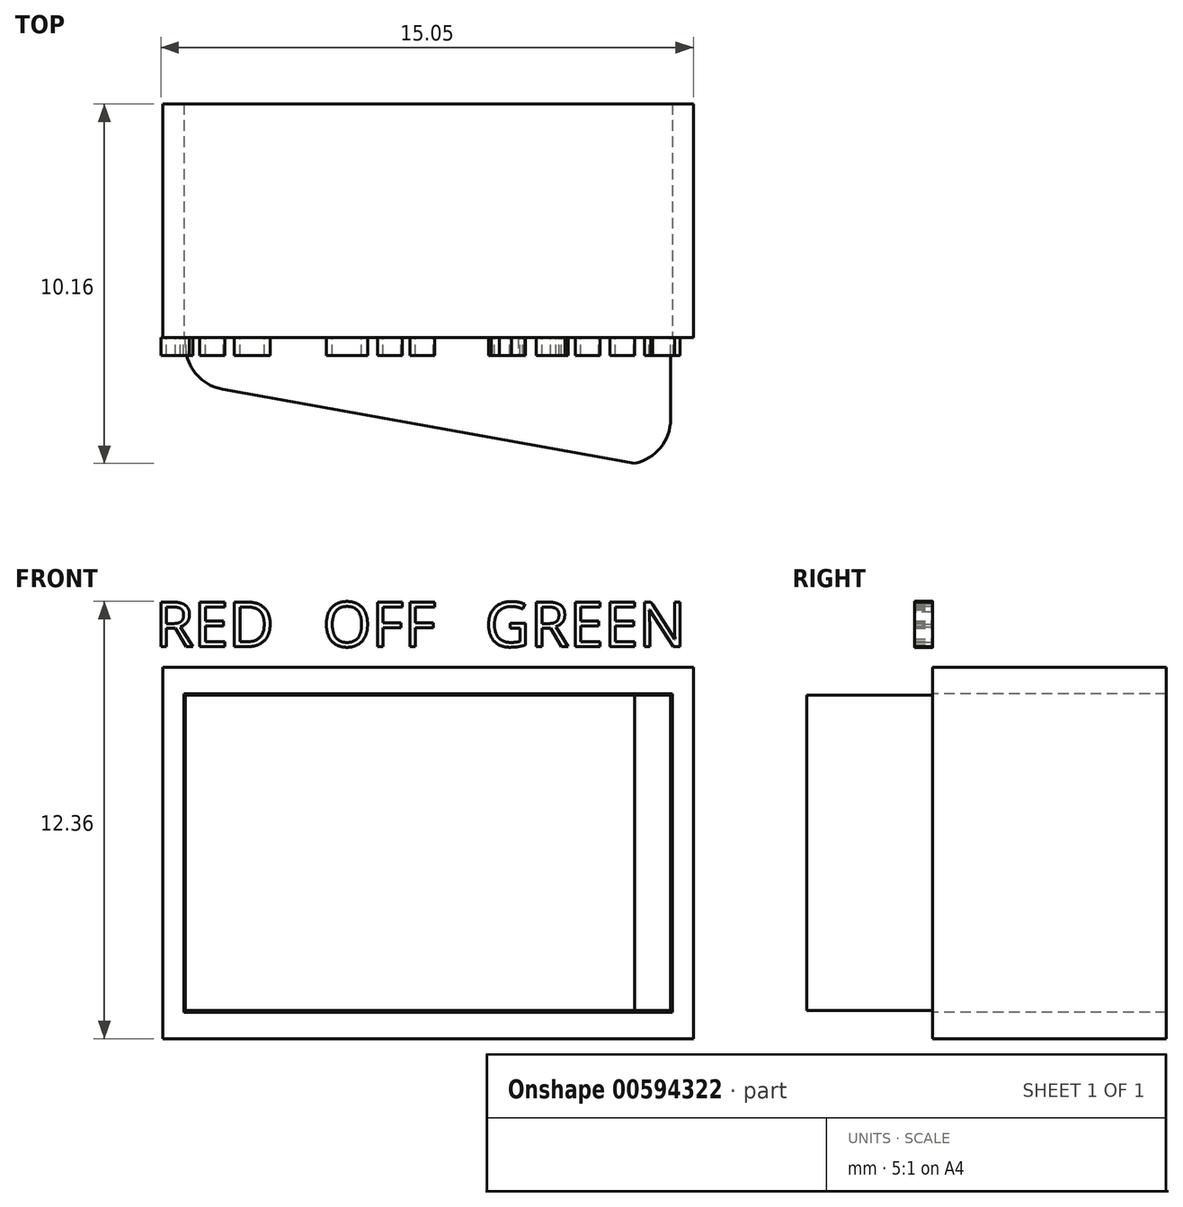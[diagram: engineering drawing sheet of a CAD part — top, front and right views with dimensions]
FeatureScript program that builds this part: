
annotation { "Feature Type Name" : "Feature", "Feature Type Description" : "" }
export const myFeature = defineFeature(function(context is Context, id is Id, definition is map)
    precondition{}
    {
        {
            var Q0;
            Q0=qCreatedBy(makeId("Front.planeOp"),FACE);
            var sketch = newSketch(context, id + "F0", { "sketchPlane" : qUnion([Q0])});
            skLineSegment(sketch, "E0.bottom", {"start": v(-6.9, -4.5) * mm, "end": v(6.9, -4.5) * mm});
            skLineSegment(sketch, "E0.top", {"start": v(-6.9, 4.5) * mm, "end": v(6.9, 4.5) * mm});
            skLineSegment(sketch, "E0.left", {"start": v(-6.9, -4.5) * mm, "end": v(-6.9, 4.5) * mm});
            skLineSegment(sketch, "E0.right", {"start": v(6.9, -4.5) * mm, "end": v(6.9, 4.5) * mm});
            skPoint(sketch, "E0.middle", {"position": v(0, 0) * mm});
            skLineSegment(sketch, "E1.bottom", {"start": v(-7.5, -5.25) * mm, "end": v(7.5, -5.25) * mm});
            skLineSegment(sketch, "E1.top", {"start": v(-7.5, 5.25) * mm, "end": v(7.5, 5.25) * mm});
            skLineSegment(sketch, "E1.left", {"start": v(-7.5, -5.25) * mm, "end": v(-7.5, 5.25) * mm});
            skLineSegment(sketch, "E1.right", {"start": v(7.5, -5.25) * mm, "end": v(7.5, 5.25) * mm});
            skSolve(sketch);
        }
        {
            var Q0;
            Q0=makeQuery(id+"F0.imprint","IMPRINT",FACE,{"disambiguationData":[TD([[makeQuery(id+"F0.imprint","IMPRINT",EDGE,{"derivedFrom":sQuery(id+"F0.wireOp",EDGE,"E0.bottom")}),-1.0]])]});
            extrude(context, id + "F1", {"entities" : qUnion([Q0]), "oppositeDirection" : true, "depth" : 6.6 * mm, "offsetDistance" : 25.4 * mm});
        }
        {
            var Q0;
            Q0=qCreatedBy(makeId("Front.planeOp"),FACE);
            var sketch = newSketch(context, id + "F2", { "sketchPlane" : qUnion([Q0])});
            skLineSegment(sketch, "E2.bottom", {"start": v(6.86, -4.46) * mm, "end": v(-6.86, -4.46) * mm});
            skLineSegment(sketch, "E2.top", {"start": v(6.86, 4.46) * mm, "end": v(-6.86, 4.46) * mm});
            skLineSegment(sketch, "E2.left", {"start": v(6.86, -4.46) * mm, "end": v(6.86, 4.46) * mm});
            skLineSegment(sketch, "E2.right", {"start": v(-6.86, -4.46) * mm, "end": v(-6.86, 4.46) * mm});
            skPoint(sketch, "E2.middle", {"position": v(0, 0) * mm});
            skSolve(sketch);
        }
        {
            var Q0;
            Q0=makeQuery(id+"F2.imprint","IMPRINT",FACE,{"disambiguationData":[TD([[makeQuery(id+"F2.imprint","IMPRINT",EDGE,{"derivedFrom":sQuery(id+"F2.wireOp",EDGE,"E2.bottom")}),-1.0]])]});
            extrude(context, id + "F3", {"entities" : qUnion([Q0]), "depth" : 3.56 * mm, "offsetDistance" : 25.4 * mm});
        }
        {
            var Q0;
            Q0=makeQuery(id+"F3.opExtrude","CAP_EDGE",EDGE,{"disambiguationData":[OSD([sQuery(id+"F2.wireOp",EDGE,"E2.right")])],"isStart":false});
            chamfer(context, id + "F4", {"entities" : qUnion([Q0]), "chamferType" : ChamferType.TWO_OFFSETS, "width1" : 2.3 * mm, "oppositeDirection" : false, "width2" : 12.7 * mm, "tangentPropagation" : true});
        }
        {
            var Q0;
            {var subQ0=sQuery(id+"F2.wireOp",EDGE,"E2.right");Q0=makeQuery(id+"F4.opChamfer","BLEND_EDGE",EDGE,{"blendedFrom":[makeQuery(id+"F3.opExtrude","CAP_EDGE",EDGE,{"disambiguationData":[OSD([subQ0])],"isStart":false}),makeQuery(id+"F3.opExtrude","SWEPT_FACE",FACE,{"disambiguationData":[OSD([subQ0])]})],"blendedInto":[makeQuery(id+"F3.opExtrude","SWEPT_FACE",FACE,{"disambiguationData":[OSD([subQ0])]})]});}
            var Q1;
            Q1=makeQuery(id+"F3.opExtrude","CAP_EDGE",EDGE,{"disambiguationData":[OSD([sQuery(id+"F2.wireOp",EDGE,"E2.left")])],"isStart":false});
            fillet(context, id + "F5", {"entities" : qUnion([Q0, Q1]), "radius" : 1.27 * mm, "tangentPropagation" : true, "allowEdgeOverflow" : false});
        }
        {
            var Q0;
            Q0=qCreatedBy(makeId("Front.planeOp"),FACE);
            var sketch = newSketch(context, id + "F6", { "sketchPlane" : qUnion([Q0])});
            skText(sketch, "E3", { "text": "RED   OFF   GREEN", "fontName": "NotoSans-Regular.ttf"});
            const initialGuessF6  = {"E3": [-0.00772, 0.00583, 1, 0, 0.00127]};
            skSetInitialGuess(sketch, initialGuessF6);
            skSolve(sketch);
        }
        {
            var Q0;
            Q0 = qSketchRegion(id + "F6", true);
            extrude(context, id + "F7", {"entities" : qUnion([Q0]), "depth" : 0.5 * mm, "offsetDistance" : 25.4 * mm});
        }
    });
